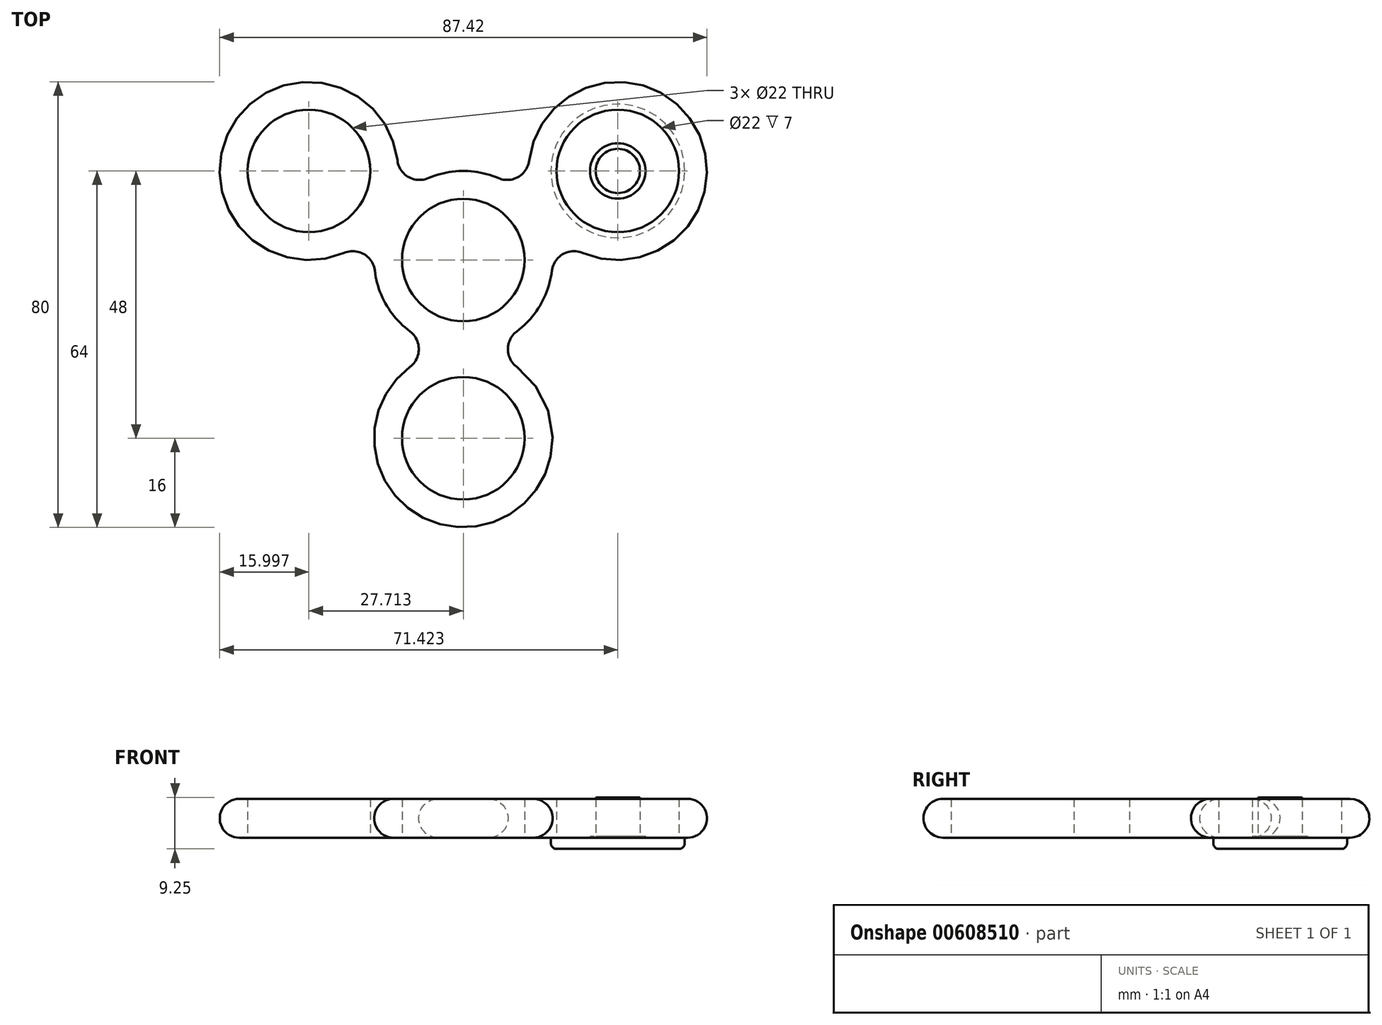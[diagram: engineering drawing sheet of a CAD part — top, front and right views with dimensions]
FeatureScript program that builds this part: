
annotation { "Feature Type Name" : "Feature", "Feature Type Description" : "" }
export const myFeature = defineFeature(function(context is Context, id is Id, definition is map)
    precondition{}
    {
        {
            var Q0;
            Q0=qCreatedBy(makeId("Top.planeOp"),FACE);
            var sketch = newSketch(context, id + "F0", { "sketchPlane" : qUnion([Q0])});
            skCircle(sketch, "E0", {"center": v(0, 0) * mm, "radius": 11 * mm});
            skCircle(sketch, "E1", {"center": v(0, 0) * mm, "radius": 3.98 * mm});
            skCircle(sketch, "E2", {"center": v(0, 0) * mm, "radius": 16 * mm});
            skLineSegment(sketch, "E3", {"start": v(0, 0) * mm, "end": v(0, -32) * mm});
            skLineSegment(sketch, "E4", {"start": v(0, 0) * mm, "end": v(27.71, 16) * mm});
            skLineSegment(sketch, "E5", {"start": v(0, 0) * mm, "end": v(-27.71, 16) * mm});
            skCircle(sketch, "E6", {"center": v(27.71, 16) * mm, "radius": 3.98 * mm});
            skCircle(sketch, "E7", {"center": v(-27.71, 16) * mm, "radius": 3.98 * mm});
            skCircle(sketch, "E8", {"center": v(0, -32) * mm, "radius": 3.98 * mm});
            skCircle(sketch, "E9", {"center": v(0, -32) * mm, "radius": 11 * mm});
            skCircle(sketch, "E10", {"center": v(27.71, 16) * mm, "radius": 11 * mm});
            skCircle(sketch, "E11", {"center": v(-27.71, 16) * mm, "radius": 11 * mm});
            skCircle(sketch, "E12", {"center": v(27.71, 16) * mm, "radius": 16 * mm});
            skCircle(sketch, "E13", {"center": v(-27.71, 16) * mm, "radius": 16 * mm});
            skCircle(sketch, "E14", {"center": v(0, -32) * mm, "radius": 16 * mm});
            skArc(sketch, "E15", {"start": v(21.43, 1.29) * mm, "mid": v(17.86, 1.07) * mm, "end": v(15.89, -1.91) * mm});
            skArc(sketch, "E16", {"start": v(6.29, 14.71) * mm, "mid": v(9.86, 14.93) * mm, "end": v(11.83, 17.91) * mm});
            skArc(sketch, "E17", {"start": v(-11.83, 17.91) * mm, "mid": v(-9.86, 14.93) * mm, "end": v(-6.29, 14.71) * mm});
            skArc(sketch, "E18", {"start": v(-15.89, -1.91) * mm, "mid": v(-17.86, 1.07) * mm, "end": v(-21.43, 1.29) * mm});
            skArc(sketch, "E19", {"start": v(-9.6, -19.2) * mm, "mid": v(-8, -16) * mm, "end": v(-9.6, -12.8) * mm});
            skArc(sketch, "E20", {"start": v(9.6, -12.8) * mm, "mid": v(8, -16) * mm, "end": v(9.6, -19.2) * mm});
            skSolve(sketch);
        }
        {
            var Q0;
            Q0 = qSketchRegion(id + "F0", true);
            extrude(context, id + "F1", {"entities" : qUnion([Q0]), "depth" : 7 * mm, "offsetDistance" : 25 * mm});
        }
        {
            var Q0;
            Q0=makeQuery(id+"F1.opExtrude","CAP_EDGE",EDGE,{"disambiguationData":[OSD([sQuery(id+"F0.wireOp",EDGE,"E15")])],"isStart":false});
            var Q1;
            Q1=makeQuery(id+"F1.opExtrude","CAP_EDGE",EDGE,{"disambiguationData":[OSD([sQuery(id+"F0.wireOp",EDGE,"E15")])],"isStart":true});
            fillet(context, id + "F2", {"entities" : qUnion([Q0, Q1]), "radius" : 3.5 * mm, "tangentPropagation" : true, "allowEdgeOverflow" : false});
        }
        {
            var Q0;
            Q0=qCreatedBy(makeId("Top.planeOp"),FACE);
            var sketch = newSketch(context, id + "F3", { "sketchPlane" : qUnion([Q0])});
            skCircle(sketch, "E21.0", {"center": v(0, 0) * mm, "radius": 11 * mm});
            skCircle(sketch, "E21.1", {"center": v(0, 0) * mm, "radius": 3.98 * mm});
            skCircle(sketch, "E21.2", {"center": v(0, 0) * mm, "radius": 16 * mm});
            skLineSegment(sketch, "E21.3", {"start": v(0, 0) * mm, "end": v(0, -32) * mm});
            skLineSegment(sketch, "E21.4", {"start": v(0, 0) * mm, "end": v(27.71, 16) * mm});
            skLineSegment(sketch, "E21.5", {"start": v(0, 0) * mm, "end": v(-27.71, 16) * mm});
            skCircle(sketch, "E21.6", {"center": v(27.71, 16) * mm, "radius": 3.98 * mm});
            skCircle(sketch, "E21.7", {"center": v(-27.71, 16) * mm, "radius": 3.98 * mm});
            skCircle(sketch, "E21.8", {"center": v(0, -32) * mm, "radius": 3.98 * mm});
            skCircle(sketch, "E21.9", {"center": v(0, -32) * mm, "radius": 11 * mm});
            skCircle(sketch, "E21.10", {"center": v(27.71, 16) * mm, "radius": 11 * mm});
            skCircle(sketch, "E21.11", {"center": v(-27.71, 16) * mm, "radius": 11 * mm});
            skCircle(sketch, "E21.12", {"center": v(27.71, 16) * mm, "radius": 16 * mm});
            skCircle(sketch, "E21.13", {"center": v(-27.71, 16) * mm, "radius": 16 * mm});
            skCircle(sketch, "E21.14", {"center": v(0, -32) * mm, "radius": 16 * mm});
            skArc(sketch, "E21.15", {"start": v(21.43, 1.29) * mm, "mid": v(17.86, 1.07) * mm, "end": v(15.89, -1.91) * mm});
            skArc(sketch, "E21.16", {"start": v(6.29, 14.71) * mm, "mid": v(9.86, 14.93) * mm, "end": v(11.83, 17.91) * mm});
            skArc(sketch, "E21.17", {"start": v(-11.83, 17.91) * mm, "mid": v(-9.86, 14.93) * mm, "end": v(-6.29, 14.71) * mm});
            skArc(sketch, "E21.18", {"start": v(-15.89, -1.91) * mm, "mid": v(-17.86, 1.07) * mm, "end": v(-21.43, 1.29) * mm});
            skArc(sketch, "E21.19", {"start": v(-9.6, -19.2) * mm, "mid": v(-8, -16) * mm, "end": v(-9.6, -12.8) * mm});
            skArc(sketch, "E21.20", {"start": v(9.6, -12.8) * mm, "mid": v(8, -16) * mm, "end": v(9.6, -19.2) * mm});
            skCircle(sketch, "E22.0", {"center": v(27.71, 16) * mm, "radius": 4.98 * mm});
            skCircle(sketch, "E23.0", {"center": v(27.71, 16) * mm, "radius": 12 * mm});
            skCircle(sketch, "E24.0", {"center": v(27.71, 16) * mm, "radius": 2.48 * mm});
            skSolve(sketch);
        }
        {
            var Q0;
            Q0=makeQuery(id+"F3.imprint","IMPRINT",FACE,{"disambiguationData":[TD([[makeQuery(id+"F3.imprint","IMPRINT",EDGE,{"derivedFrom":sQuery(id+"F3.wireOp",EDGE,"E21.6")}),1.0]])]});
            extrude(context, id + "F4", {"entities" : qUnion([Q0]), "depth" : 7.25 * mm, "offsetDistance" : 25 * mm});
        }
        {
            var Q0;
            Q0=makeQuery(id+"F3.imprint","IMPRINT",FACE,{"disambiguationData":[TD([[makeQuery(id+"F3.imprint","IMPRINT",EDGE,{"derivedFrom":sQuery(id+"F3.wireOp",EDGE,"E21.6")}),-1.0]])]});
            var Q1;
            Q1=makeQuery(id+"F3.imprint","IMPRINT",FACE,{"disambiguationData":[TD([[makeQuery(id+"F3.imprint","IMPRINT",EDGE,{"derivedFrom":sQuery(id+"F3.wireOp",EDGE,"E21.6")}),1.0]])]});
            extrude(context, id + "F5", {"entities" : qUnion([Q0, Q1]), "operationType" : NewBodyOperationType.ADD, "depth" : .25 * mm, "offsetDistance" : 25 * mm});
        }
        {
            var Q0;
            Q0=makeQuery(id+"F3.imprint","IMPRINT",FACE,{"disambiguationData":[TD([[makeQuery(id+"F3.imprint","IMPRINT",EDGE,{"derivedFrom":sQuery(id+"F3.wireOp",EDGE,"E21.10")}),-1.0]])]});
            var Q1;
            Q1=makeQuery(id+"F3.imprint","IMPRINT",FACE,{"disambiguationData":[TD([[makeQuery(id+"F3.imprint","IMPRINT",EDGE,{"derivedFrom":sQuery(id+"F3.wireOp",EDGE,"E21.10")}),1.0]])]});
            var Q2;
            Q2=makeQuery(id+"F3.imprint","IMPRINT",FACE,{"disambiguationData":[TD([[makeQuery(id+"F3.imprint","IMPRINT",EDGE,{"derivedFrom":sQuery(id+"F3.wireOp",EDGE,"E21.6")}),1.0]])]});
            var Q3;
            Q3=makeQuery(id+"F3.imprint","IMPRINT",FACE,{"disambiguationData":[TD([[makeQuery(id+"F3.imprint","IMPRINT",EDGE,{"derivedFrom":sQuery(id+"F3.wireOp",EDGE,"E21.6")}),-1.0]])]});
            var Q4;
            Q4=makeQuery(id+"F3.imprint","IMPRINT",FACE,{"disambiguationData":[TD([[makeQuery(id+"F3.imprint","IMPRINT",EDGE,{"derivedFrom":sQuery(id+"F3.wireOp",EDGE,"E24.0")}),1.0]])]});
            extrude(context, id + "F6", {"entities" : qUnion([Q0, Q1, Q2, Q3, Q4]), "operationType" : NewBodyOperationType.ADD, "oppositeDirection" : true, "depth" : 2 * mm, "offsetDistance" : 25 * mm});
        }
        {
            var Q0;
            Q0=makeQuery(id+"F6.opExtrude","CAP_EDGE",EDGE,{"disambiguationData":[OSD([sQuery(id+"F3.wireOp",EDGE,"E23.0")])],"isStart":false});
            var Q1;
            Q1=makeQuery(id+"F6.opExtrude","CAP_EDGE",EDGE,{"disambiguationData":[OSD([sQuery(id+"F3.wireOp",EDGE,"E23.0")])],"isStart":true});
            fillet(context, id + "F7", {"entities" : qUnion([Q0, Q1]), "radius" : 1 * mm, "tangentPropagation" : true, "allowEdgeOverflow" : false});
        }
        {
            var Q0;
            Q0=makeQuery(id+"F3.imprint","IMPRINT",FACE,{"disambiguationData":[TD([[makeQuery(id+"F3.imprint","IMPRINT",EDGE,{"derivedFrom":sQuery(id+"F3.wireOp",EDGE,"E24.0")}),1.0]])]});
            extrude(context, id + "F8", {"entities" : qUnion([Q0]), "depth" : 7.25 * mm, "offsetDistance" : 25 * mm});
        }
        {
            var Q0;
            Q0=makeQuery(id+"F3.imprint","IMPRINT",FACE,{"disambiguationData":[TD([[makeQuery(id+"F3.imprint","IMPRINT",EDGE,{"derivedFrom":sQuery(id+"F3.wireOp",EDGE,"E21.6")}),-1.0]])]});
            var Q1;
            Q1=makeQuery(id+"F3.imprint","IMPRINT",FACE,{"disambiguationData":[TD([[makeQuery(id+"F3.imprint","IMPRINT",EDGE,{"derivedFrom":sQuery(id+"F3.wireOp",EDGE,"E21.6")}),1.0]])]});
            var Q2;
            Q2=makeQuery(id+"F3.imprint","IMPRINT",FACE,{"disambiguationData":[TD([[makeQuery(id+"F3.imprint","IMPRINT",EDGE,{"derivedFrom":sQuery(id+"F3.wireOp",EDGE,"E24.0")}),1.0]])]});
            extrude(context, id + "F9", {"entities" : qUnion([Q0, Q1, Q2]), "operationType" : NewBodyOperationType.ADD, "depth" : 0.25 * mm, "offsetDistance" : 25 * mm});
        }
        {
            var Q0;
            Q0=makeQuery(id+"F3.imprint","IMPRINT",FACE,{"disambiguationData":[TD([[makeQuery(id+"F3.imprint","IMPRINT",EDGE,{"derivedFrom":sQuery(id+"F3.wireOp",EDGE,"E21.10")}),-1.0]])]});
            var Q1;
            Q1=makeQuery(id+"F3.imprint","IMPRINT",FACE,{"disambiguationData":[TD([[makeQuery(id+"F3.imprint","IMPRINT",EDGE,{"derivedFrom":sQuery(id+"F3.wireOp",EDGE,"E21.10")}),1.0]])]});
            var Q2;
            Q2=makeQuery(id+"F3.imprint","IMPRINT",FACE,{"disambiguationData":[TD([[makeQuery(id+"F3.imprint","IMPRINT",EDGE,{"derivedFrom":sQuery(id+"F3.wireOp",EDGE,"E21.6")}),-1.0]])]});
            var Q3;
            Q3=makeQuery(id+"F3.imprint","IMPRINT",FACE,{"disambiguationData":[TD([[makeQuery(id+"F3.imprint","IMPRINT",EDGE,{"derivedFrom":sQuery(id+"F3.wireOp",EDGE,"E21.6")}),1.0]])]});
            var Q4;
            Q4=makeQuery(id+"F3.imprint","IMPRINT",FACE,{"disambiguationData":[TD([[makeQuery(id+"F3.imprint","IMPRINT",EDGE,{"derivedFrom":sQuery(id+"F3.wireOp",EDGE,"E24.0")}),1.0]])]});
            extrude(context, id + "F10", {"entities" : qUnion([Q0, Q1, Q2, Q3, Q4]), "operationType" : NewBodyOperationType.ADD, "oppositeDirection" : true, "depth" : 2 * mm, "offsetDistance" : 25 * mm});
        }
        {
            var Q0;
            Q0=makeQuery(id+"F10.opExtrude","CAP_EDGE",EDGE,{"disambiguationData":[OSD([sQuery(id+"F3.wireOp",EDGE,"E23.0")])],"isStart":false});
            var Q1;
            Q1=makeQuery(id+"F10.opExtrude","CAP_EDGE",EDGE,{"disambiguationData":[OSD([sQuery(id+"F3.wireOp",EDGE,"E23.0")])],"isStart":true});
            fillet(context, id + "F11", {"entities" : qUnion([Q0, Q1]), "radius" : 1 * mm, "tangentPropagation" : true, "allowEdgeOverflow" : false});
        }
    });
